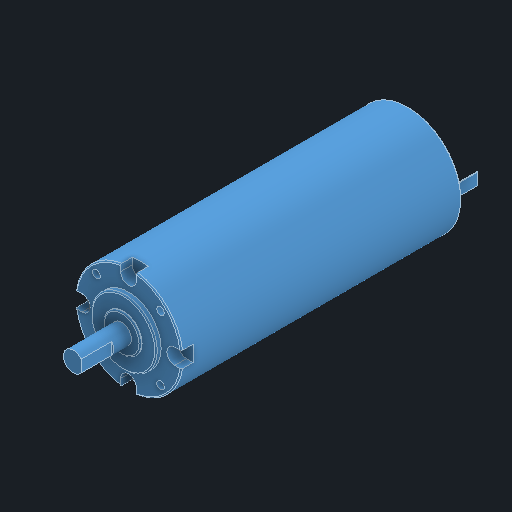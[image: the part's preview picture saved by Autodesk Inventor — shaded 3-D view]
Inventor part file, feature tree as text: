
AUTODESK INVENTOR PART (.ipt)
format: ipt  version: 2024 (Build 280153000, 153)  size: 269,824 bytes
history: native  units: mm
features: extrude x11, sketch x11, pattern_circular x2, other x1, fillet x1, chamfer x1
ambient origin geometry x8: Origin, YZ Plane, XZ Plane, XY Plane, X Axis, Y Axis, Z Axis, Center Point
bodies: Body1 (feature_tree)
feature tree (27):
  other  "Твердое тело1"
  extrude  "Выдавливание1"  Depth=42.0mm
  extrude  "Выдавливание2"  Depth=110.0mm TaperAngle=0.0deg
  extrude  "Выдавливание3"  Depth=25.7mm
  pattern_circular  "Круговой массив1"  [2 undecoded]
  extrude  "Выдавливание4"  Depth=6.2mm
  pattern_circular  "Круговой массив2"  [2 undecoded]
  extrude  "Выдавливание5"  Depth=4.6mm TaperAngle=0.0deg
  extrude  "Выдавливание6"  Depth=40.0mm TaperAngle=360.0deg
  extrude  "Выдавливание7"  Depth=3.0mm
  extrude  "Выдавливание8"  Depth=3.2mm
  extrude  "Выдавливание9"  Depth=7.0mm TaperAngle=0.0deg
  extrude  "Выдавливание10"  Depth=40.0mm TaperAngle=360.0deg
  extrude  "Выдавливание11"  Depth=14.7mm
  fillet  "Сопряжение1"  Radius=0.7mm
  chamfer  "Фаска1"  Distance=7.8mm
  sketch  "Эскиз1"
  sketch  "Эскиз2"
  sketch  "Эскиз3"
  sketch  "Эскиз4"
  sketch  "Эскиз5"
  sketch  "Эскиз6"
  sketch  "Эскиз7"
  sketch  "Эскиз8"
  sketch  "Эскиз9"
  sketch  "Эскиз10"
  sketch  "Эскиз11"
note: 4 required parameter values undecoded (feature->parameter linkage not recoverable at this tier; creation-order binding heuristic only, values carry confidence <= 0.55)
